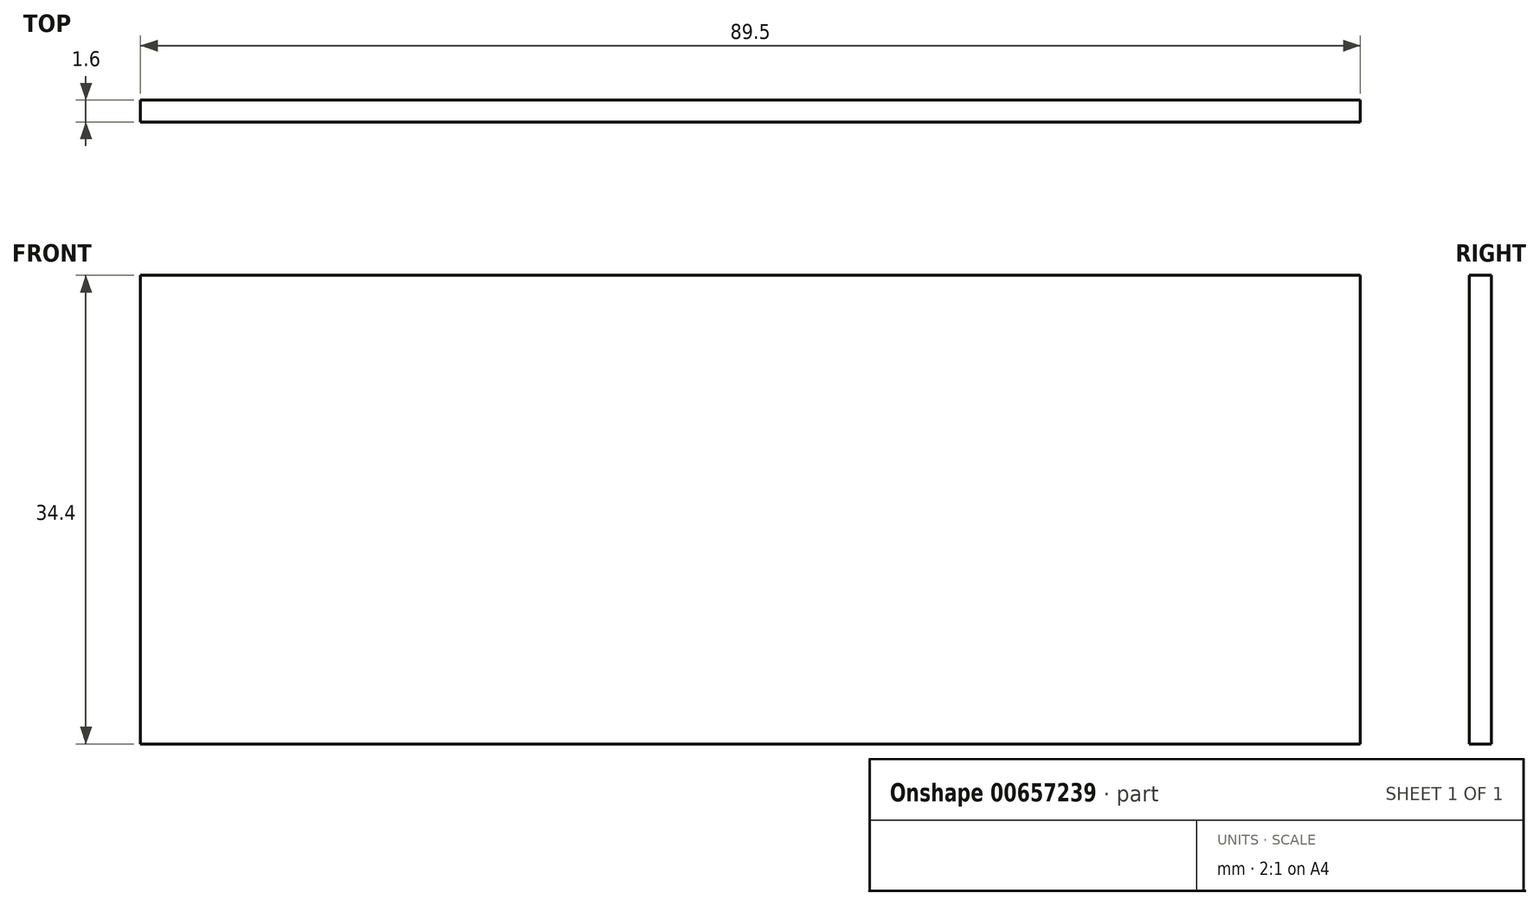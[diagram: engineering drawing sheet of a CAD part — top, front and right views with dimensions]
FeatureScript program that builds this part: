
annotation { "Feature Type Name" : "Feature", "Feature Type Description" : "" }
export const myFeature = defineFeature(function(context is Context, id is Id, definition is map)
    precondition{}
    {
        {
            var Q0;
            Q0=qCreatedBy(makeId("Front.planeOp"),FACE);
            var sketch = newSketch(context, id + "F0", { "sketchPlane" : qUnion([Q0])});
            skLineSegment(sketch, "E0.bottom", {"start": v(-44.75, 17.2) * mm, "end": v(44.75, 17.2) * mm});
            skLineSegment(sketch, "E0.top", {"start": v(-44.75, -17.2) * mm, "end": v(44.75, -17.2) * mm});
            skLineSegment(sketch, "E0.left", {"start": v(-44.75, 17.2) * mm, "end": v(-44.75, -17.2) * mm});
            skLineSegment(sketch, "E0.right", {"start": v(44.75, 17.2) * mm, "end": v(44.75, -17.2) * mm});
            skPoint(sketch, "E0.middle", {"position": v(0, 0) * mm});
            skSolve(sketch);
        }
        {
            var Q0;
            Q0 = qSketchRegion(id + "F0", true);
            extrude(context, id + "F1", {"entities" : qUnion([Q0]), "depth" : 1.6 * mm, "offsetDistance" : 25 * mm});
        }
    });
